# Revit family: 706520001_Dispensador de Jabón Expuesto
name_source: partatom
category: Plumbing Fixtures
units: mm (PartAtom-declared; Revit-internal decimal feet)

## family parameters
Always vertical = Yes
Cut with Voids When Loaded = No
Host = Wall
OmniClass Number = 23.31.25.29.13
OmniClass Title = Hand Soap Dispensers
Part Type = Normal
Room Calculation Point = No
Round Connector Dimension = Use Diameter
Shared = No

## types (1)
- Type 1
    Alto = 320 mm  [stored 1.04987 ft]
    Ancho = 110 mm
    Capacidad de carga = 1 Litro de jabón
    Colección = Descarga Muro
    Creado por = BIMBAU
    Default Elevation = 0 mm  [stored 0 ft]
    Description = El baño de tu empresa tendrá lo mejor con este dispensador de jabón expuesto de accionamiento tipo push.
    Fecha de creación = 15/04/2021
    Garantía = 10 Años
    Línea = Dispensadores de Jabón
    Manufacturer = Corona
    Material = Corona_Plastico_Blanco
    Material 2 = Corona_Plastico_Gris
    Profundidad = 111 mm
    Referencia = 706520001
    Resistencia = Resistente a la corrosión pelado y decoloración por agua Resistente al efecto de jabones y limpiadores de tocador
    Tipo de instalación = A pared
    URL = https://corona.co
    Uso = Institucional

note: [stored X ft] marks values corroborated as IEEE doubles in the binary element streams (Revit-internal decimal feet)

## geometry (parser evidence)
native form markers: Sweep x6
no freeform markers — native parametric forms only
